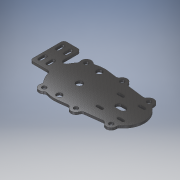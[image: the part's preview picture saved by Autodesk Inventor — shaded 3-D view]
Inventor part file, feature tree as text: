
AUTODESK INVENTOR PART (.ipt)
format: ipt  version: 2017 (Build 210142000, 142)  size: 386,560 bytes
history: native  units: mm
features: extrude x6, sketch x6, fillet x2, other x1
ambient origin geometry x8: Origin, YZ Plane, XZ Plane, XY Plane, X Axis, Y Axis, Z Axis, Center Point
bodies: Body1 (feature_tree)
feature tree (15):
  other  "Sólido1"
  extrude  "Extrusión1"  Depth=88.9mm
  extrude  "Extrusión2"  Depth=22.225mm
  fillet  "Empalme1"  Radius=22.225mm
  extrude  "Extrusión3"  Depth=22.225mm
  extrude  "Extrusión4"  TaperAngle=0.0deg  [1 undecoded]
  extrude  "Extrusión5"  Depth=5.0mm TaperAngle=0.0deg
  fillet  "Empalme2"  Radius=9.525mm
  extrude  "Extrusión6"  Depth=5.55625mm
  sketch  "Boceto1"  dims[d0=114.3mm d1=88.9mm]
  sketch  "Boceto2"  dims[d2=203.2mm d3=22.225mm d4=22.225mm]
  sketch  "Boceto3"  dims[d7=22.225mm d8=22.225mm]
  sketch  "Boceto4"  dims[d11=22.225mm d13=0.0mm]
  sketch  "Boceto5"  dims[d14=22.225mm d16=5.0mm d17=0.0mm d18=9.525mm]
  sketch  "Boceto6"  dims[d19=9.525mm d20=9.525mm d21=9.525mm d22=9.525mm d23=9.525mm d24=25.4mm d25=0.0mm d26=6.35mm d27=12.7mm d28=12.7mm d29=44.45mm d30=44.45mm d31=31.75mm d32=31.75mm d33=14.2875mm d34=12.7mm d35=12.7mm d36=45.0mm d37=45.0mm d38=25.4mm d39=0.0mm d40=12.7mm d41=56.0mm d42=56.0mm d43=28.0mm d44=28.0mm d45=0.0mm d46=93.4212mm d47=47.5mm d48=47.5mm d49=23.75mm d50=23.75mm d57=5.55625mm d58=5.159375mm d59=5.55625mm d60=5.55625mm d61=5.159375mm d62=5.159375mm d63=5.55625mm d64=5.159375mm d65=0.0mm d66=5.55625mm d67=5.55625mm d68=5.159375mm d69=5.159375mm d70=0.0mm d71=5.55625mm d72=5.55625mm d73=5.159375mm d74=5.159375mm d75=0.0mm d76=25.4mm d77=0.0mm d78=12.7mm d79=12.7mm d80=5.159375mm d81=5.159375mm d82=247.65mm d83=76.2mm d84=123.825mm d85=38.1mm d86=25.4mm d87=25.4mm d88=0.0mm d89=0.0mm d90=6.35mm d91=7.9375mm d92=18.25625mm d93=10.06475mm d94=7.9375mm d95=7.9375mm d96=5.55625mm d97=5.55625mm d98=0.0mm d99=0.0mm d100=7.9375mm d101=10.06475mm d102=18.25625mm d103=7.9375mm d104=7.9375mm d105=5.55625mm d106=5.55625mm d107=0.0mm d108=0.0mm d109=7.9375mm d110=18.25625mm d111=10.06475mm d112=7.9375mm d113=7.9375mm d114=5.55625mm d115=5.55625mm d116=0.0mm d117=0.0mm d118=7.9375mm d119=18.25625mm d120=10.06475mm d121=7.9375mm d122=7.9375mm d123=5.55625mm d124=5.55625mm d125=0.0mm d126=0.0mm d127=25.4mm d128=0.0mm]
note: 1 required parameter value undecoded (feature->parameter linkage not recoverable at this tier; creation-order binding heuristic only, values carry confidence <= 0.55)
